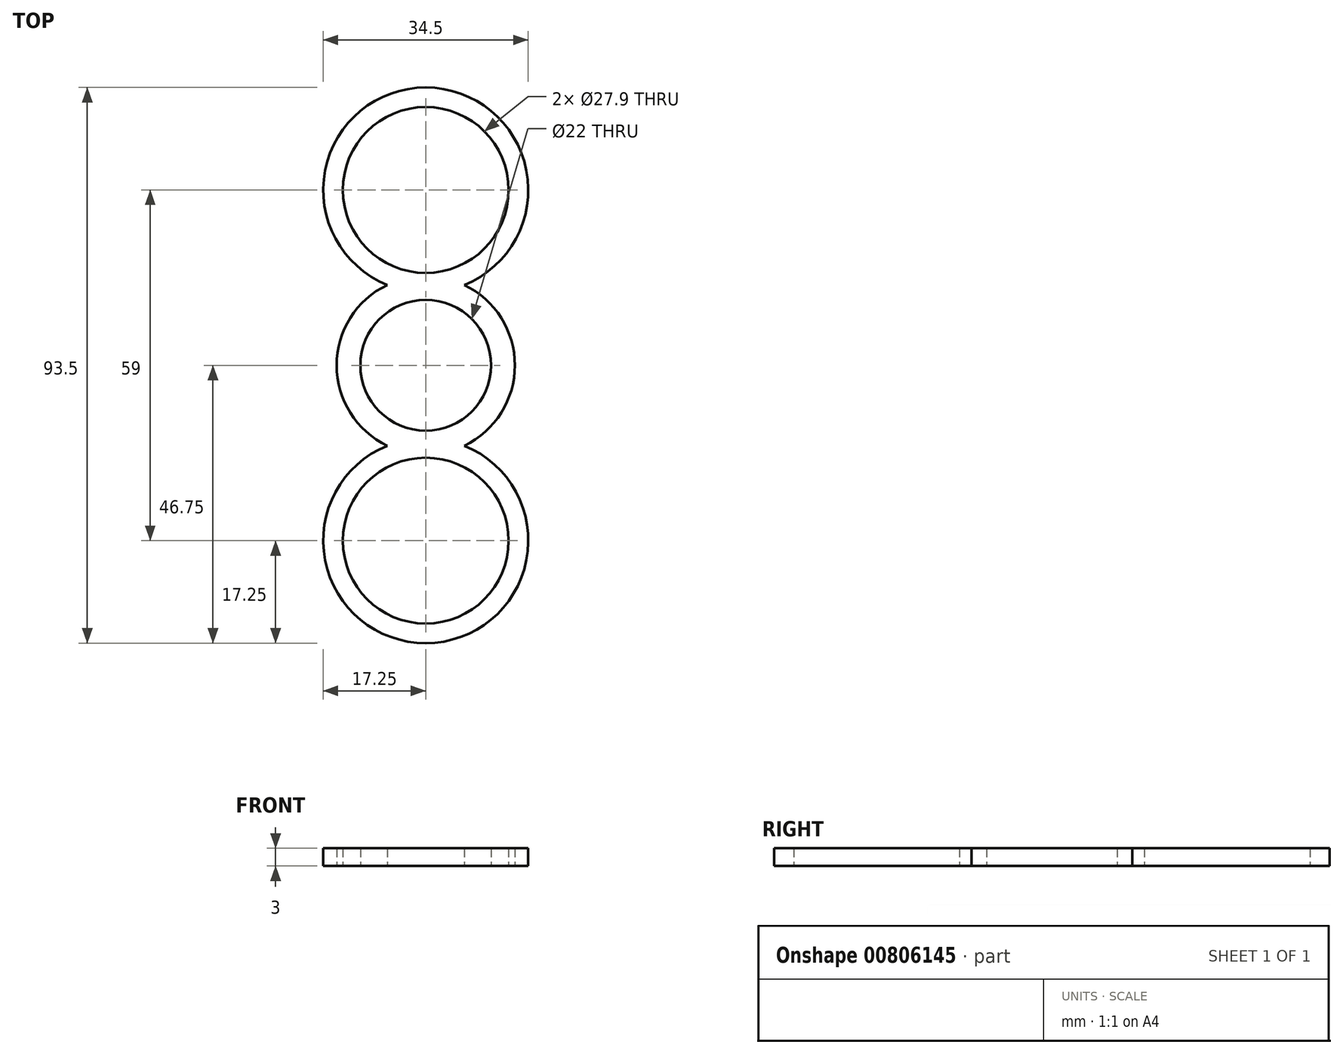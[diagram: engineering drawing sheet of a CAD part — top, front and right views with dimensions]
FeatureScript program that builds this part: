
annotation { "Feature Type Name" : "Feature", "Feature Type Description" : "" }
export const myFeature = defineFeature(function(context is Context, id is Id, definition is map)
    precondition{}
    {
        {
            var Q0;
            Q0=qCreatedBy(makeId("Top.planeOp"),FACE);
            var sketch = newSketch(context, id + "F0", { "sketchPlane" : qUnion([Q0])});
            skArc(sketch, "E0", {"start": v(11, 0) * mm, "mid": v(0, 11) * mm, "end": v(-11, 0) * mm});
            skArc(sketch, "E1", {"start": v(-6.5, 13.52) * mm, "mid": v(-12.7, 7.99) * mm, "end": v(-15, 0) * mm});
            skLineSegment(sketch, "E2", {"start": v(0, 0) * mm, "end": v(0, 29.5) * mm});
            skCircle(sketch, "E3", {"center": v(0, 29.5) * mm, "radius": 13.95 * mm});
            skArc(sketch, "E4", {"start": v(6.5, 13.52) * mm, "mid": v(0, 46.75) * mm, "end": v(-6.5, 13.52) * mm});
            skArc(sketch, "E5.trimOffspring", {"start": v(15, 0) * mm, "mid": v(12.7, 7.99) * mm, "end": v(6.5, 13.52) * mm});
            skArc(sketch, "E6.1.0", {"start": v(-6.5, -13.52) * mm, "mid": v(0, -46.75) * mm, "end": v(6.5, -13.52) * mm});
            skCircle(sketch, "E6.1.1", {"center": v(0, -29.5) * mm, "radius": 13.95 * mm});
            skArc(sketch, "E6.1.2", {"start": v(6.5, -13.52) * mm, "mid": v(12.7, -7.99) * mm, "end": v(15, 0) * mm});
            skArc(sketch, "E6.1.3", {"start": v(-11, 0) * mm, "mid": v(0, -11) * mm, "end": v(11, 0) * mm});
            skArc(sketch, "E6.1.4", {"start": v(-15, 0) * mm, "mid": v(-12.7, -7.99) * mm, "end": v(-6.5, -13.52) * mm});
            skSolve(sketch);
        }
        {
            var Q0;
            Q0 = qSketchRegion(id + "F0", true);
            extrude(context, id + "F1", {"entities" : qUnion([Q0]), "depth" : 3 * mm, "offsetDistance" : 25 * mm});
        }
    });
